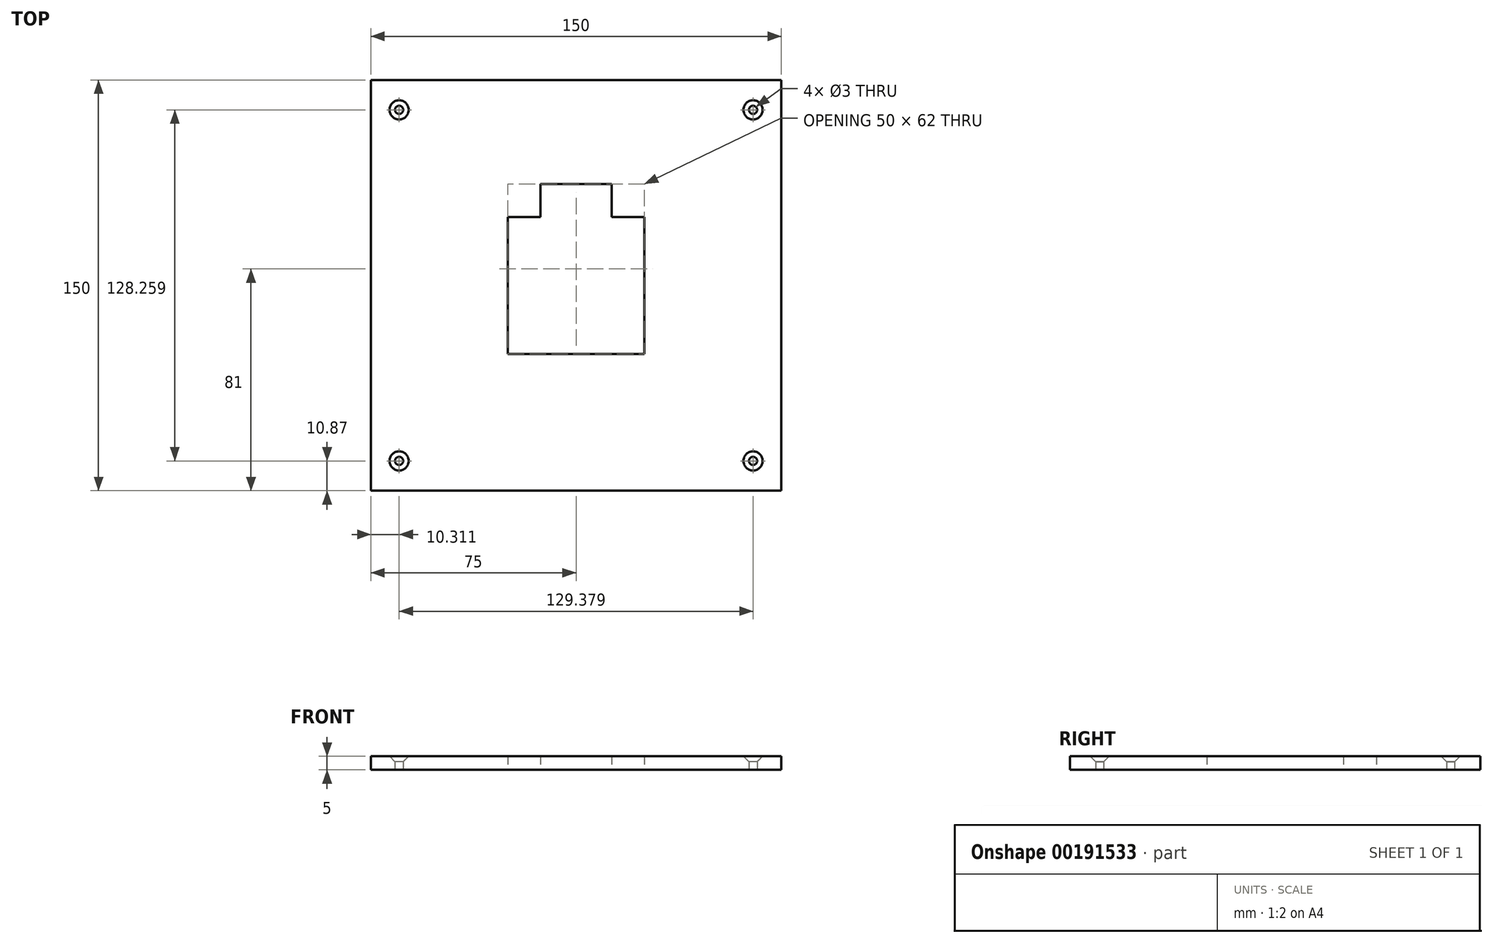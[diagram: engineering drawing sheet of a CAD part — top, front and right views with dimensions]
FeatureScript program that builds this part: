
annotation { "Feature Type Name" : "Feature", "Feature Type Description" : "" }
export const myFeature = defineFeature(function(context is Context, id is Id, definition is map)
    precondition{}
    {
        {
            var Q0;
            Q0=qCreatedBy(makeId("Top.planeOp"),FACE);
            var sketch = newSketch(context, id + "F0", { "sketchPlane" : qUnion([Q0])});
            skLineSegment(sketch, "E0.bottom", {"start": v(-25, 25) * mm, "end": v(-13, 25) * mm});
            skLineSegment(sketch, "E0.top", {"start": v(-25, -25) * mm, "end": v(25, -25) * mm});
            skLineSegment(sketch, "E0.left", {"start": v(-25, 25) * mm, "end": v(-25, -25) * mm});
            skLineSegment(sketch, "E0.right", {"start": v(25, 25) * mm, "end": v(25, -25) * mm});
            skLineSegment(sketch, "E1.top", {"start": v(-13, 37) * mm, "end": v(13, 37) * mm});
            skLineSegment(sketch, "E1.left", {"start": v(-13, 25) * mm, "end": v(-13, 37) * mm});
            skLineSegment(sketch, "E1.right", {"start": v(13, 25) * mm, "end": v(13, 37) * mm});
            skLineSegment(sketch, "E2.trimOffspring", {"start": v(13, 25) * mm, "end": v(25, 25) * mm});
            skLineSegment(sketch, "E3.bottom", {"start": v(-75, 75) * mm, "end": v(75, 75) * mm});
            skLineSegment(sketch, "E3.top", {"start": v(-75, -75) * mm, "end": v(75, -75) * mm});
            skLineSegment(sketch, "E3.left", {"start": v(-75, 75) * mm, "end": v(-75, -75) * mm});
            skLineSegment(sketch, "E3.right", {"start": v(75, 75) * mm, "end": v(75, -75) * mm});
            skCircle(sketch, "E4", {"center": v(-64.69, 64.13) * mm, "radius": 1.5 * mm});
            skCircle(sketch, "E5.MirrorC", {"center": v(64.69, 64.13) * mm, "radius": 1.5 * mm});
            skCircle(sketch, "E6.MirrorC", {"center": v(-64.69, -64.13) * mm, "radius": 1.5 * mm});
            skCircle(sketch, "E7.MirrorC", {"center": v(64.69, -64.13) * mm, "radius": 1.5 * mm});
            skSolve(sketch);
        }
        {
            var Q0;
            Q0=makeQuery(id+"F0.imprint","IMPRINT",FACE,{"disambiguationData":[TD([[makeQuery(id+"F0.imprint","IMPRINT",EDGE,{"derivedFrom":sQuery(id+"F0.wireOp",EDGE,"E0.bottom")}),1.0]])]});
            extrude(context, id + "F1", {"entities" : qUnion([Q0]), "depth" : 5 * mm});
        }
        {
            var Q0;
            Q0=makeQuery(id+"F1.opExtrude","CAP_EDGE",EDGE,{"disambiguationData":[OSD([sQuery(id+"F0.wireOp",EDGE,"E4")])],"isStart":false});
            var Q1;
            Q1=makeQuery(id+"F1.opExtrude","CAP_EDGE",EDGE,{"disambiguationData":[OSD([sQuery(id+"F0.wireOp",EDGE,"E6.MirrorC")])],"isStart":false});
            var Q2;
            Q2=makeQuery(id+"F1.opExtrude","CAP_EDGE",EDGE,{"disambiguationData":[OSD([sQuery(id+"F0.wireOp",EDGE,"E7.MirrorC")])],"isStart":false});
            var Q3;
            Q3=makeQuery(id+"F1.opExtrude","CAP_EDGE",EDGE,{"disambiguationData":[OSD([sQuery(id+"F0.wireOp",EDGE,"E5.MirrorC")])],"isStart":false});
            chamfer(context, id + "F2", {"entities" : qUnion([Q0, Q1, Q2, Q3]), "width" : 2 * mm, "tangentPropagation" : true});
        }
    });
